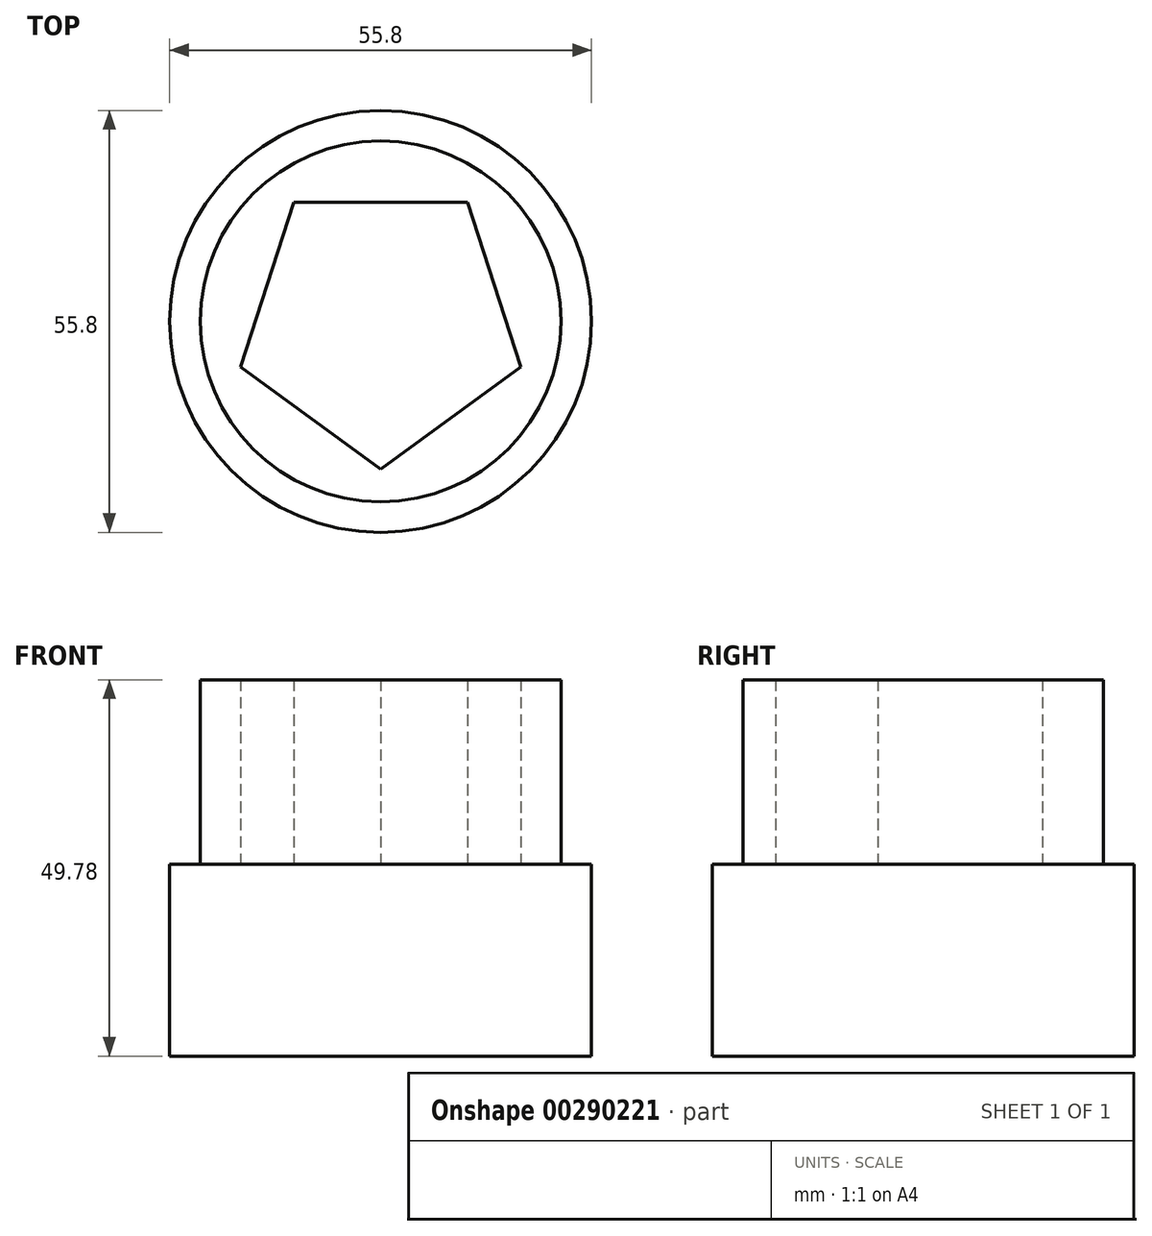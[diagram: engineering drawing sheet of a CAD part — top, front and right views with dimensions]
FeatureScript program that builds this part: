
annotation { "Feature Type Name" : "Feature", "Feature Type Description" : "" }
export const myFeature = defineFeature(function(context is Context, id is Id, definition is map)
    precondition{}
    {
        {
            var Q0;
            Q0=qCreatedBy(makeId("Top.planeOp"),FACE);
            var sketch = newSketch(context, id + "F0", { "sketchPlane" : qUnion([Q0])});
            skCircle(sketch, "E0", {"center": v(0, 0) * mm, "radius": 27.9 * mm});
            skSolve(sketch);
        }
        {
            var Q0;
            Q0 = qSketchRegion(id + "F0", true);
            extrude(context, id + "F1", {"entities" : qUnion([Q0]), "depth" : 25.4 * mm});
        }
        {
            var Q0;
            Q0=makeQuery(id+"F1.opExtrude","CAP_FACE",FACE,{"disambiguationData":[OSD([sQuery(id+"F0.wireOp",EDGE,"E0")])],"isStart":false});
            var sketch = newSketch(context, id + "F2", { "sketchPlane" : qUnion([Q0])});
            skCircle(sketch, "E1", {"center": v(0, 0) * mm, "radius": 23.86 * mm});
            skCircle(sketch, "E2.cCircle", {"center": v(0, 0) * mm, "radius": 15.8 * mm, "construction": true});
            skLineSegment(sketch, "E2.0", {"start": v(-11.47, 15.8) * mm, "end": v(11.47, 15.8) * mm});
            skLineSegment(sketch, "E2.1", {"start": v(11.47, 15.8) * mm, "end": v(18.56, -6.03) * mm});
            skLineSegment(sketch, "E2.2", {"start": v(18.56, -6.03) * mm, "end": v(0, -19.52) * mm});
            skLineSegment(sketch, "E2.3", {"start": v(0, -19.52) * mm, "end": v(-18.56, -6.03) * mm});
            skLineSegment(sketch, "E2.4", {"start": v(-18.56, -6.03) * mm, "end": v(-11.47, 15.8) * mm});
            skPoint(sketch, "E2.0.midPoint", {"position": v(0, 15.8) * mm});
            skSolve(sketch);
        }
        {
            var Q0;
            Q0 = qSketchRegion(id + "F2", true);
            extrude(context, id + "F3", {"entities" : qUnion([Q0]), "operationType" : NewBodyOperationType.ADD, "depth" : 24.38 * mm});
        }
    });
